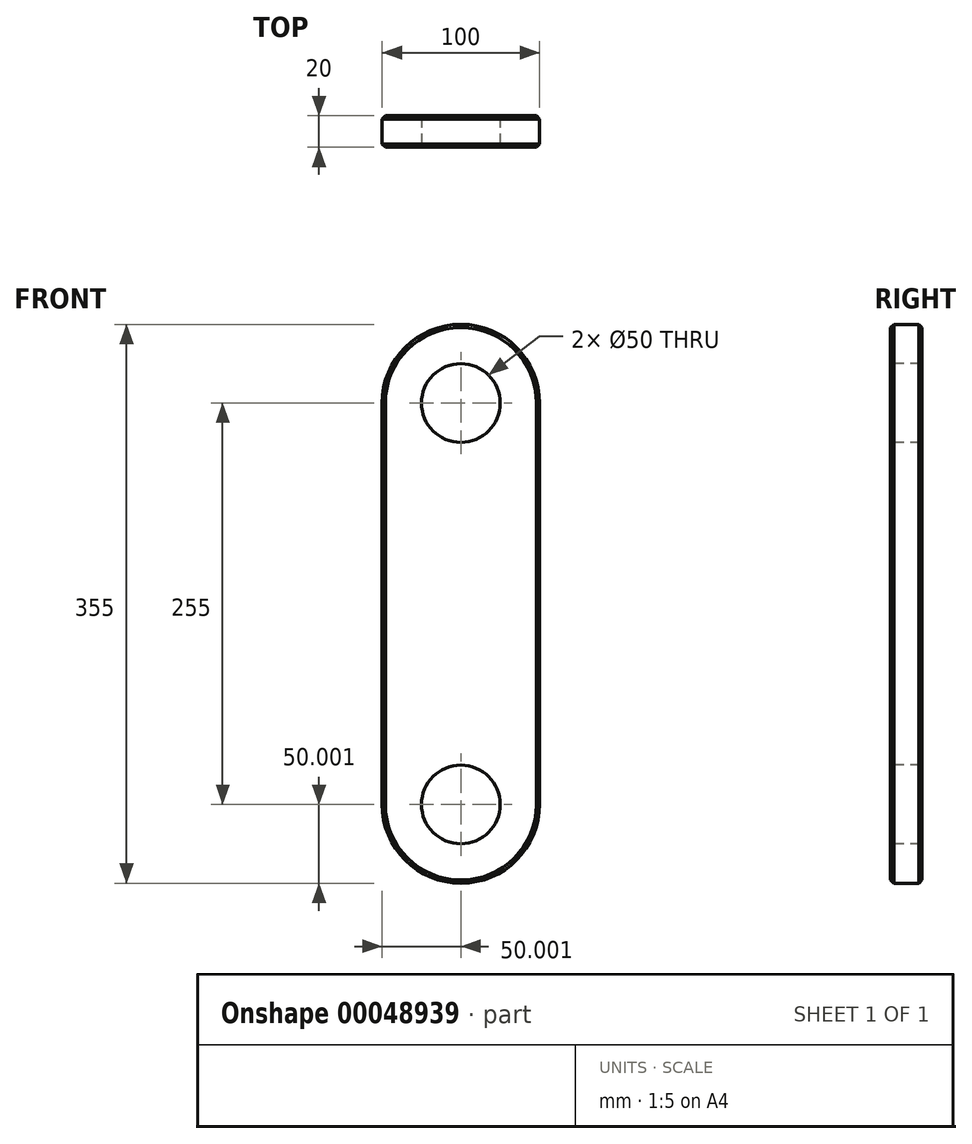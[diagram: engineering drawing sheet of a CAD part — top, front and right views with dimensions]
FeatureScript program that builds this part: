
annotation { "Feature Type Name" : "Feature", "Feature Type Description" : "" }
export const myFeature = defineFeature(function(context is Context, id is Id, definition is map)
    precondition{}
    {
        {
            var Q0;
            Q0=qCreatedBy(makeId("Front.planeOp"),FACE);
            var sketch = newSketch(context, id + "F0", { "sketchPlane" : qUnion([Q0])});
            skLineSegment(sketch, "E0", {"start": v(-89, 112.84) * mm, "end": v(-89, -142.16) * mm});
            skLineSegment(sketch, "E1", {"start": v(11, 112.84) * mm, "end": v(11, -142.16) * mm});
            skArc(sketch, "E2", {"start": v(11, 112.84) * mm, "mid": v(-39, 162.84) * mm, "end": v(-89, 112.84) * mm});
            skArc(sketch, "E3", {"start": v(-89, -142.16) * mm, "mid": v(-39, -192.16) * mm, "end": v(11, -142.16) * mm});
            skCircle(sketch, "E4", {"center": v(-39, 112.84) * mm, "radius": 25 * mm});
            skCircle(sketch, "E5", {"center": v(-39, -142.16) * mm, "radius": 25 * mm});
            skSolve(sketch);
        }
        {
            var Q0;
            Q0=makeQuery(id+"F0.imprint","IMPRINT",FACE,{"disambiguationData":[TD([[makeQuery(id+"F0.imprint","IMPRINT",EDGE,{"derivedFrom":sQuery(id+"F0.wireOp",EDGE,"E0")}),1.0]])]});
            extrude(context, id + "F1", {"entities" : qUnion([Q0]), "oppositeDirection" : true, "depth" : 20 * mm});
        }
        {
            var Q0;
            Q0=makeQuery(id+"F1.opExtrude","CAP_EDGE",EDGE,{"disambiguationData":[OSD([sQuery(id+"F0.wireOp",EDGE,"E1")])],"isStart":true});
            var Q1;
            Q1=makeQuery(id+"F1.opExtrude","CAP_EDGE",EDGE,{"disambiguationData":[OSD([sQuery(id+"F0.wireOp",EDGE,"E1")])],"isStart":false});
            var Q2;
            Q2=makeQuery(id+"F1.opExtrude","CAP_EDGE",EDGE,{"disambiguationData":[OSD([sQuery(id+"F0.wireOp",EDGE,"E2")])],"isStart":false});
            var Q3;
            Q3=makeQuery(id+"F1.opExtrude","CAP_EDGE",EDGE,{"disambiguationData":[OSD([sQuery(id+"F0.wireOp",EDGE,"E2")])],"isStart":true});
            var Q4;
            Q4=makeQuery(id+"F1.opExtrude","CAP_EDGE",EDGE,{"disambiguationData":[OSD([sQuery(id+"F0.wireOp",EDGE,"E0")])],"isStart":false});
            var Q5;
            Q5=makeQuery(id+"F1.opExtrude","CAP_EDGE",EDGE,{"disambiguationData":[OSD([sQuery(id+"F0.wireOp",EDGE,"E3")])],"isStart":false});
            var Q6;
            Q6=makeQuery(id+"F1.opExtrude","CAP_EDGE",EDGE,{"disambiguationData":[OSD([sQuery(id+"F0.wireOp",EDGE,"E3")])],"isStart":true});
            var Q7;
            Q7=makeQuery(id+"F1.opExtrude","CAP_EDGE",EDGE,{"disambiguationData":[OSD([sQuery(id+"F0.wireOp",EDGE,"E0")])],"isStart":true});
            chamfer(context, id + "F2", {"entities" : qUnion([Q0, Q1, Q2, Q3, Q4, Q5, Q6, Q7]), "chamferType" : ChamferType.OFFSET_ANGLE, "width" : 2 * mm, "oppositeDirection" : false, "angle" : 45 * degree, "tangentPropagation" : true});
        }
    });
